annotation { "Feature Type Name" : "Feature", "Feature Type Description" : "" }
export const myFeature = defineFeature(function(context is Context, id is Id, definition is map)
    precondition{}
    {
        {
            var Q0;
            Q0=qCreatedBy(makeId("Front.planeOp"),FACE);
            var sketch = newSketch(context, id + "F0", { "sketchPlane" : qUnion([Q0])});
            skLineSegment(sketch, "E0", {"start": v(0, 0) * mm, "end": v(-4876.8, 0) * mm});
            skLineSegment(sketch, "E1", {"start": v(0, 0) * mm, "end": v(0, 3048) * mm});
            skLineSegment(sketch, "E2", {"start": v(0, 3048) * mm, "end": v(-4876.8, 0) * mm});
            skLineSegment(sketch, "E3", {"start": v(-4876.8, 0) * mm, "end": v(-4876.8, -6096) * mm});
            skLineSegment(sketch, "E4", {"start": v(0, 0) * mm, "end": v(4876.8, 0) * mm});
            skLineSegment(sketch, "E5", {"start": v(0, 3048) * mm, "end": v(4876.8, 0) * mm});
            skLineSegment(sketch, "E6", {"start": v(4876.8, 0) * mm, "end": v(4876.8, -6096) * mm});
            skLineSegment(sketch, "E7", {"start": v(-4876.8, -6096) * mm, "end": v(4876.8, -6096) * mm});
            skLineSegment(sketch, "E8", {"start": v(0, -6096) * mm, "end": v(-457.2, -6096) * mm});
            skLineSegment(sketch, "E9", {"start": v(0, -6096) * mm, "end": v(457.2, -6096) * mm});
            skLineSegment(sketch, "E10", {"start": v(457.2, -6096) * mm, "end": v(457.2, -3962.4) * mm});
            skLineSegment(sketch, "E11", {"start": v(457.2, -3962.4) * mm, "end": v(-457.2, -3962.4) * mm});
            skLineSegment(sketch, "E12", {"start": v(-457.2, -3962.4) * mm, "end": v(-457.2, -6096) * mm});
            skText(sketch, "E13", { "text": "Dylan Kuehnel", "fontName": "Arimo-Regular.ttf"});
            skLineSegment(sketch, "E14.bottom", {"start": v(-3810, -2438.4) * mm, "end": v(-1371.6, -2438.4) * mm});
            skLineSegment(sketch, "E14.top", {"start": v(-3810, -4267.2) * mm, "end": v(-1371.6, -4267.2) * mm});
            skLineSegment(sketch, "E14.left", {"start": v(-3810, -2438.4) * mm, "end": v(-3810, -4267.2) * mm});
            skLineSegment(sketch, "E14.right", {"start": v(-1371.6, -2438.4) * mm, "end": v(-1371.6, -4267.2) * mm});
            skLineSegment(sketch, "E15", {"start": v(3962.4, -4267.2) * mm, "end": v(3962.4, -2438.4) * mm});
            skLineSegment(sketch, "E16", {"start": v(3962.4, -2438.4) * mm, "end": v(1371.6, -2438.4) * mm});
            skLineSegment(sketch, "E17", {"start": v(1371.6, -2438.4) * mm, "end": v(1371.6, -4267.2) * mm});
            skLineSegment(sketch, "E18", {"start": v(1371.6, -4267.2) * mm, "end": v(3962.4, -4267.2) * mm});
            const initialGuessF0  = {"E13": [-5.98001, 4.25124, 1, 0, 1.39455]};
            skSetInitialGuess(sketch, initialGuessF0);
            skSolve(sketch);
        }
        {
            var Q0;
            Q0 = qSketchRegion(id + "F0", true);
            extrude(context, id + "F1", {"entities" : qUnion([Q0]), "endBound" : BoundingType.SYMMETRIC, "depth" : 6096 * mm, "offsetDistance" : 30.48 * mm});
        }
    });